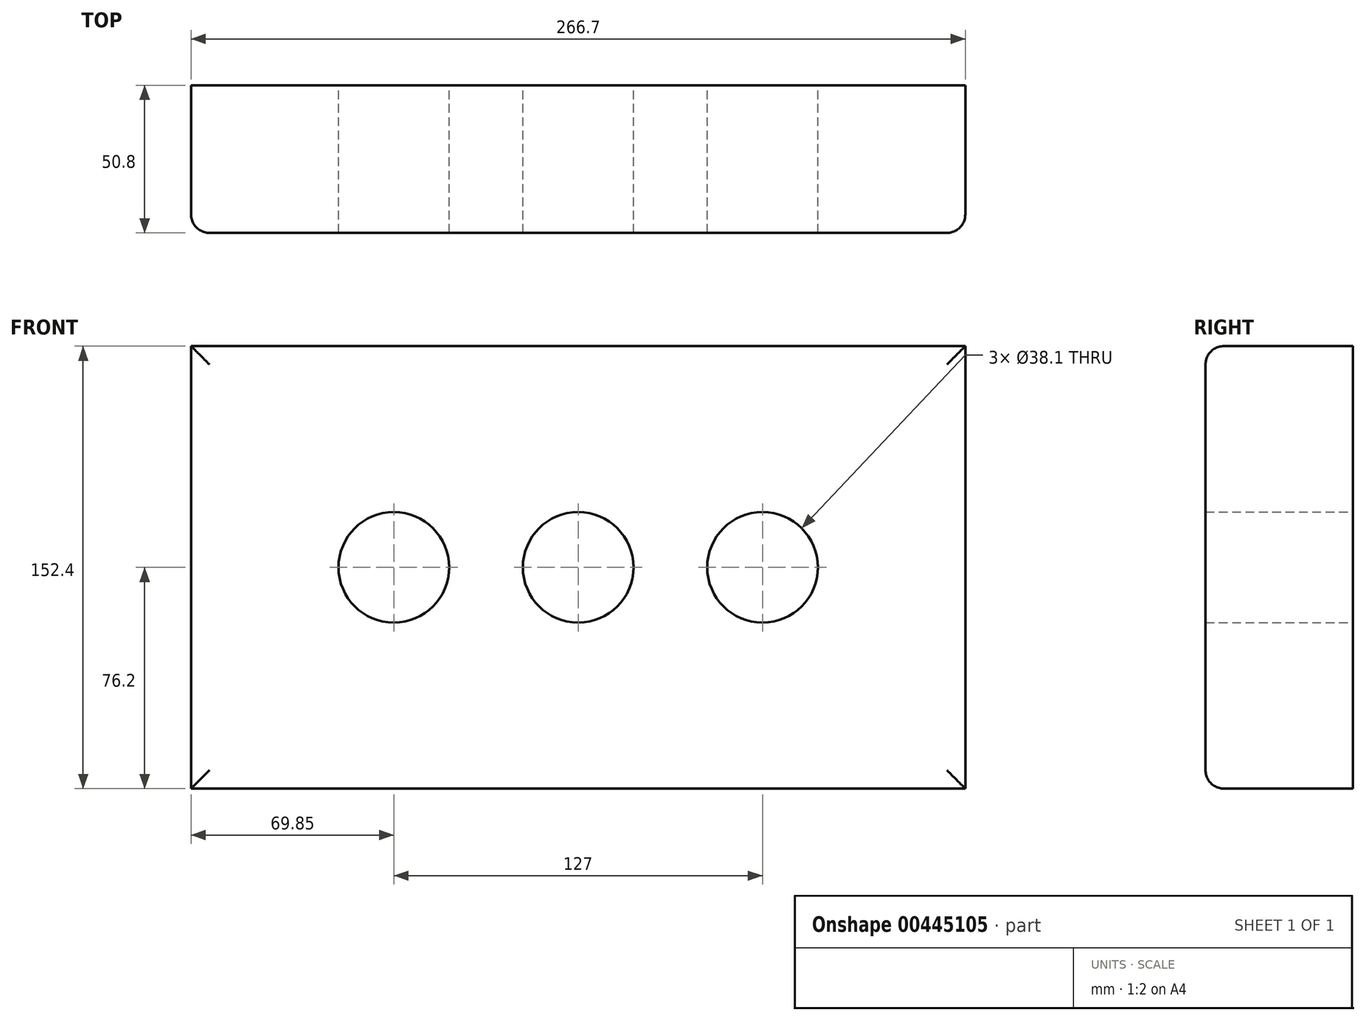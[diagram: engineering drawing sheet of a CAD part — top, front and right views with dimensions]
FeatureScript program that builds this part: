
annotation { "Feature Type Name" : "Feature", "Feature Type Description" : "" }
export const myFeature = defineFeature(function(context is Context, id is Id, definition is map)
    precondition{}
    {
        {
            var Q0;
            Q0=qCreatedBy(makeId("Front.planeOp"),FACE);
            var sketch = newSketch(context, id + "F0", { "sketchPlane" : qUnion([Q0])});
            skLineSegment(sketch, "E0.bottom", {"start": v(133.35, 76.2) * mm, "end": v(-133.35, 76.2) * mm});
            skLineSegment(sketch, "E0.top", {"start": v(133.35, -76.2) * mm, "end": v(-133.35, -76.2) * mm});
            skLineSegment(sketch, "E0.left", {"start": v(133.35, 76.2) * mm, "end": v(133.35, -76.2) * mm});
            skLineSegment(sketch, "E0.right", {"start": v(-133.35, 76.2) * mm, "end": v(-133.35, -76.2) * mm});
            skPoint(sketch, "E0.middle", {"position": v(0, 0) * mm});
            skCircle(sketch, "E1", {"center": v(0, 0) * mm, "radius": 19.05 * mm});
            skLineSegment(sketch, "E2", {"start": v(19.05, 0) * mm, "end": v(44.45, 0) * mm});
            skLineSegment(sketch, "E3", {"start": v(-19.05, 0) * mm, "end": v(-44.45, 0) * mm});
            skLineSegment(sketch, "E4", {"start": v(44.45, 0) * mm, "end": v(63.5, 0) * mm});
            skLineSegment(sketch, "E5", {"start": v(-44.45, 0) * mm, "end": v(-63.5, 0) * mm});
            skCircle(sketch, "E6", {"center": v(-63.5, 0) * mm, "radius": 19.05 * mm});
            skCircle(sketch, "E7", {"center": v(63.5, 0) * mm, "radius": 19.05 * mm});
            skSolve(sketch);
        }
        {
            var Q0;
            Q0=makeQuery(id+"F0.imprint","IMPRINT",FACE,{"disambiguationData":[TD([[makeQuery(id+"F0.imprint","IMPRINT",EDGE,{"derivedFrom":sQuery(id+"F0.wireOp",EDGE,"E0.bottom")}),1.0]])]});
            extrude(context, id + "F1", {"entities" : qUnion([Q0]), "depth" : 50.8 * mm});
        }
        {
            var Q0;
            Q0=makeQuery(id+"F1.opExtrude","CAP_EDGE",EDGE,{"disambiguationData":[OSD([sQuery(id+"F0.wireOp",EDGE,"E0.bottom")])],"isStart":false});
            var Q1;
            Q1=makeQuery(id+"F1.opExtrude","CAP_EDGE",EDGE,{"disambiguationData":[OSD([sQuery(id+"F0.wireOp",EDGE,"E0.right")])],"isStart":false});
            var Q2;
            Q2=makeQuery(id+"F1.opExtrude","CAP_EDGE",EDGE,{"disambiguationData":[OSD([sQuery(id+"F0.wireOp",EDGE,"E0.top")])],"isStart":false});
            var Q3;
            Q3=makeQuery(id+"F1.opExtrude","CAP_EDGE",EDGE,{"disambiguationData":[OSD([sQuery(id+"F0.wireOp",EDGE,"E0.left")])],"isStart":false});
            fillet(context, id + "F2", {"entities" : qUnion([Q0, Q1, Q2, Q3]), "radius" : 6.35 * mm, "tangentPropagation" : true, "allowEdgeOverflow" : false});
        }
    });
